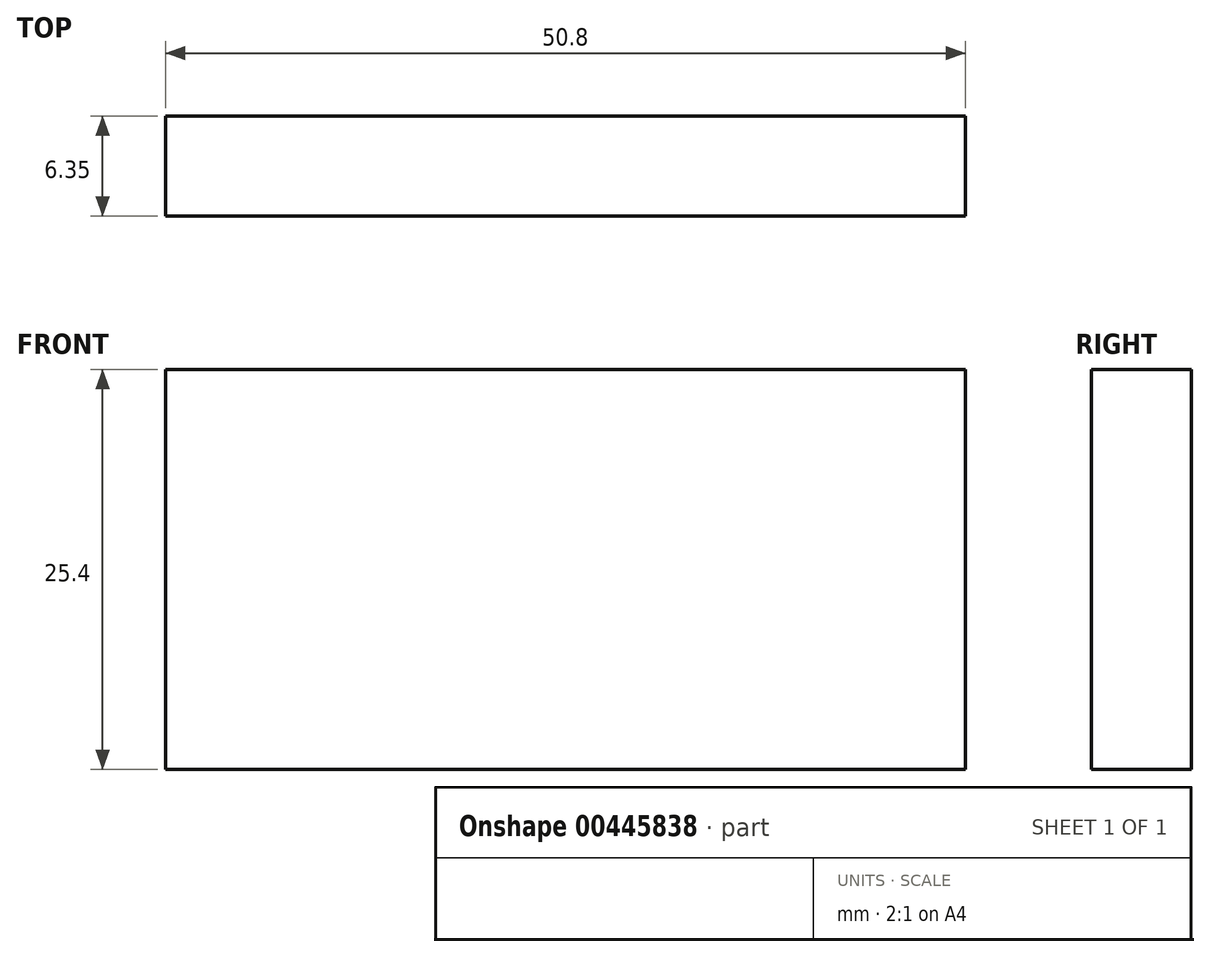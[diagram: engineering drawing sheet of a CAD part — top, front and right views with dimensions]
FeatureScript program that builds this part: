
annotation { "Feature Type Name" : "Feature", "Feature Type Description" : "" }
export const myFeature = defineFeature(function(context is Context, id is Id, definition is map)
    precondition{}
    {
        {
            var Q0;
            Q0=qCreatedBy(makeId("Front.planeOp"),FACE);
            var sketch = newSketch(context, id + "F0", { "sketchPlane" : qUnion([Q0])});
            skLineSegment(sketch, "E0.bottom", {"start": v(-41.83, 8.4) * mm, "end": v(8.97, 8.4) * mm});
            skLineSegment(sketch, "E0.top", {"start": v(-41.83, -17) * mm, "end": v(8.97, -17) * mm});
            skLineSegment(sketch, "E0.left", {"start": v(-41.83, 8.4) * mm, "end": v(-41.83, -17) * mm});
            skLineSegment(sketch, "E0.right", {"start": v(8.97, 8.4) * mm, "end": v(8.97, -17) * mm});
            skSolve(sketch);
        }
        {
            var Q0;
            Q0=makeQuery(id+"F0.imprint","IMPRINT",FACE,{"disambiguationData":[TD([[makeQuery(id+"F0.imprint","IMPRINT",EDGE,{"derivedFrom":sQuery(id+"F0.wireOp",EDGE,"E0.bottom")}),-1.0]])]});
            extrude(context, id + "F1", {"entities" : qUnion([Q0]), "depth" : 6.35 * mm});
        }
    });
